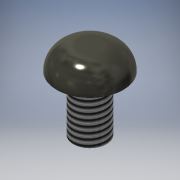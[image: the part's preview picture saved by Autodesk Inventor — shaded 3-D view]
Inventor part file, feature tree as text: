
AUTODESK INVENTOR PART (.ipt)
format: ipt  version: 2020.2 (Build 242310000, 310)  size: 142,848 bytes
history: native  units: mm
features: extrude x2, sketch x2, other x1, fillet x1, thread x1
ambient origin geometry x1: Origin
bodies: Body1 (feature_tree)
feature tree (7):
  other  "ソリッド1"
  extrude  "押し出し1"  Depth=3.0mm
  extrude  "押し出し2"  Depth=5.0mm TaperAngle=0.0deg
  fillet  "フィレット1"  Radius=6.0mm
  thread  "ねじ1"
  sketch  "スケッチ1"
  sketch  "スケッチ2"
